# Revit family: PRD_AR_WasteBins_STRATOS_WasteBin_STRX605,STRX607
name_source: partatom
category: Furniture
revit_build: Autodesk Revit 2018 (Build: 20190510_1515(x64)
units: mm (PartAtom-declared; Revit-internal decimal feet)

## family parameters
Cut with Voids When Loaded = No
Host = Face
OmniClass Number = 23.40.20.31.11
OmniClass Title = Bins
Room Calculation Point = No
Shared = No

## types (2) — shared parameters
AssetType = Fixed
BagHolder = Integrated
Category = Pr_40_50_07_96, Waste bins
Color = Stainless steel
Default Elevation = 820 mm  [stored 2.69029 ft]
DurationUnit = year
Finish = Satin finished
FinishAndColour = Stainless steel, satin finished
Form = Wall mounted
IfcExportAs = IfcFurnitureType
IfcExportType = NOTDEFINED
IntegralAccessories = includes mounting materials
Lock = key-lock
MainColor = Stainless steel
Manufacturer = KWC Group AG
ManufacturerName = KWC Group AG
ManufacturerURL = www.kwc.com
Material = Stainless steel
Materials = Stainless steel 1.4301
NBSDescription = Waste bins
NBSReference = 45-35-72/380
NominalDepth = 270 mm  [stored 0.885827 ft]
NominalHeight = 520 mm  [stored 1.70604 ft]
ProductInformation = https://pim.kwc.com
Style = Waste bin
SurfaceTreatment = InoxPlus (anti fingerprint)
URL = www.kwc.com
Uniclass2015Code = Pr_40_50_07_96
Uniclass2015Title = Waste bins
Uniclass2015Version = Products v1.7
Version = 1
WarrantyDurationUnit = year
WasteBinMaterial = PRD_AR_StainlessSteel_SatinFinished

## per-type parameters (varying)
| type | BIMObjectName | Description | Features | FillingVolume | GrossWeight | Lid | ModelNumber | Name | NetWeight | NominalLength | NominalWidth | Size |
| STRX605 | PRD_AR_WasteBins_STRATOS_WasteBin_STRX605 | Waste bin for wall mounting, stainless steel, surface satin finished, front with InoxPlus surface refinement for the reduction of finger marks and better cleaning characteristics (easy to clean), material thickness 1.5 mm, curved front cover, cylinder lock with KWC standard key, approx. 34 liter capacity, integrated bag holder, incl. stainless steel screws and dowels. | stainless steel, 1.50 mm, wall mounting, 300x520x270 mm (WxHxD) | 34.00 L | 8.06 kg | no | 2000057228 | STRATOS Waste bin STRX605 | 7.08 kg | 300 mm  [stored 0.984252 ft] | 300 mm  [stored 0.984252 ft] | 300x520x270 mm |
| STRX607 | PRD_AR_WasteBins_STRATOS_WasteBin_STRX607 | Waste bin for wall mounting, stainless steel, surface satin finished, front with InoxPlus surface refinement for the reduction of finger marks and better cleaning characteristics (easy to clean), material thickness 1.5 mm, curved front cover, cylinder lock with KWC standard key, approx. 45 liter capacity, integrated bag holder, incl. stainless steel screws and dowels. | stainless steel, 1.50 mm, wall mounting, 396x520x270 mm (WxHxD) | 45.00 L | 10.70 kg | optional | 2000057230 | STRATOS Waste bin STRX607 | 9.50 kg | 396 mm  [stored 1.29921 ft] | 396 mm  [stored 1.29921 ft] | 396x520x270 mm |

note: column(s) folded — value = type name in every type: Model, ModelReference, Type

note: [stored X ft] marks values corroborated as IEEE doubles in the binary element streams (Revit-internal decimal feet)

## geometry (parser evidence)
native form markers: Sweep x3
no freeform markers — native parametric forms only
